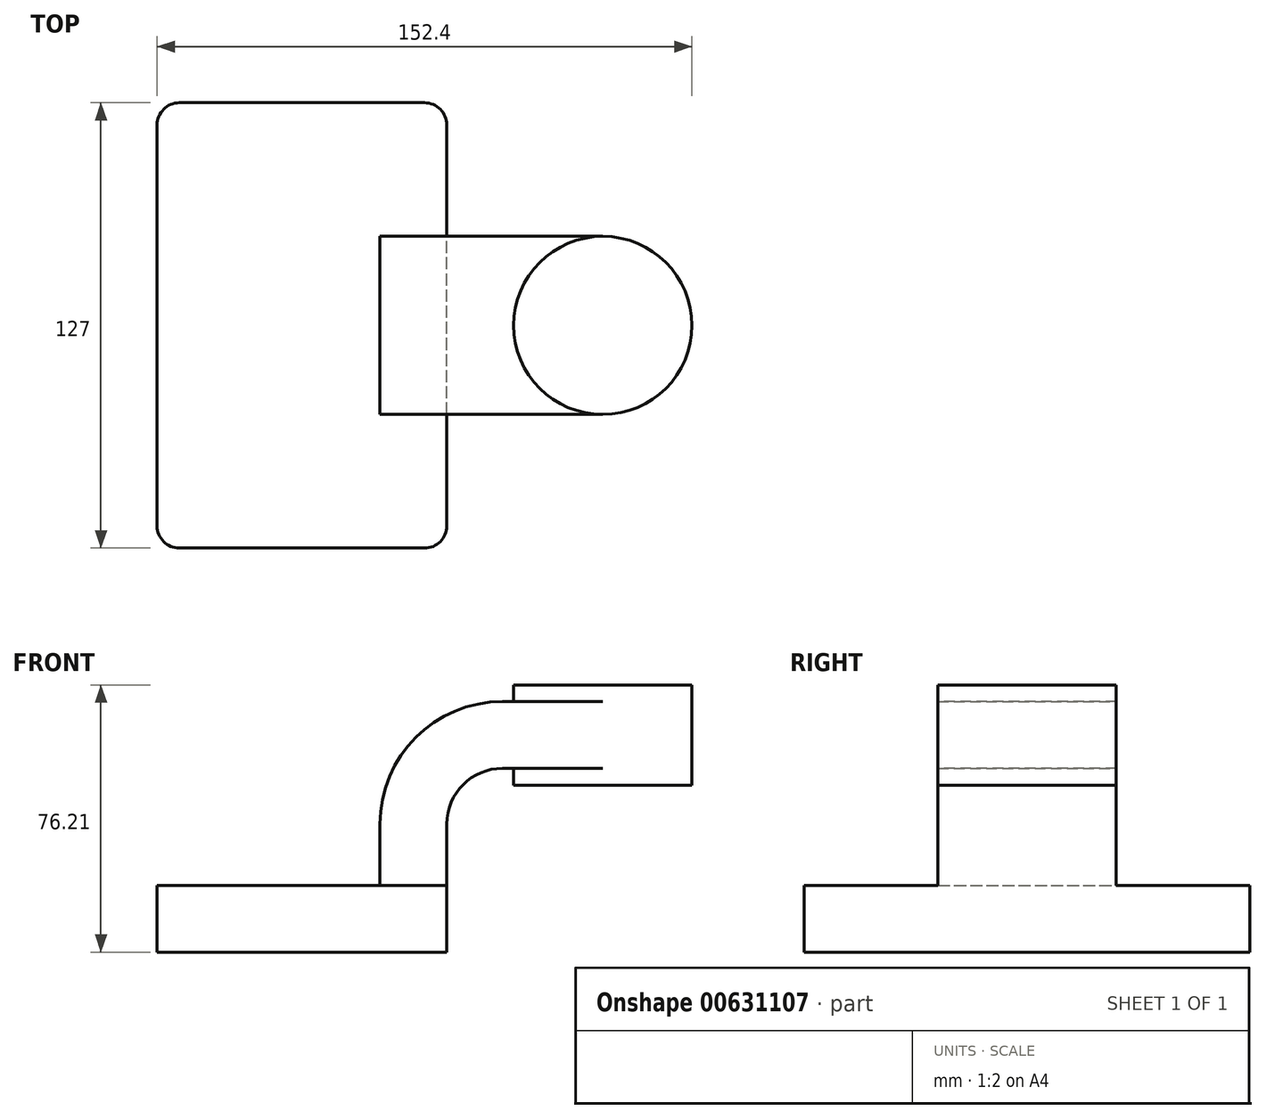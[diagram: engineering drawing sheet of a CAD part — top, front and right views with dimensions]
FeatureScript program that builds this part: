
annotation { "Feature Type Name" : "Feature", "Feature Type Description" : "" }
export const myFeature = defineFeature(function(context is Context, id is Id, definition is map)
    precondition{}
    {
        {
            var Q0;
            Q0=qCreatedBy(makeId("Front.planeOp"),FACE);
            var sketch = newSketch(context, id + "F0", { "sketchPlane" : qUnion([Q0])});
            skLineSegment(sketch, "E0.bottom", {"start": v(41.27, 9.53) * mm, "end": v(-41.28, 9.53) * mm});
            skLineSegment(sketch, "E0.top", {"start": v(41.28, -9.52) * mm, "end": v(-41.27, -9.52) * mm});
            skLineSegment(sketch, "E0.left", {"start": v(41.27, 9.53) * mm, "end": v(41.28, -9.52) * mm});
            skLineSegment(sketch, "E0.right", {"start": v(-41.28, 9.53) * mm, "end": v(-41.27, -9.52) * mm});
            skPoint(sketch, "E0.middle", {"position": v(0, 0) * mm});
            skLineSegment(sketch, "E1.bottom", {"start": v(111.12, 38.1) * mm, "end": v(60.32, 38.1) * mm});
            skLineSegment(sketch, "E1.top", {"start": v(111.12, 66.68) * mm, "end": v(60.32, 66.68) * mm});
            skLineSegment(sketch, "E1.left", {"start": v(111.12, 38.1) * mm, "end": v(111.12, 66.68) * mm});
            skLineSegment(sketch, "E1.right", {"start": v(60.32, 38.1) * mm, "end": v(60.32, 66.68) * mm});
            skPoint(sketch, "E1.middle", {"position": v(85.72, 52.39) * mm});
            skLineSegment(sketch, "E2", {"start": v(41.27, 9.53) * mm, "end": v(41.27, 27) * mm});
            skArc(sketch, "E3", {"start": v(41.27, 27) * mm, "mid": v(45.92, 38.23) * mm, "end": v(57.15, 42.88) * mm});
            skLineSegment(sketch, "E4", {"start": v(57.15, 42.88) * mm, "end": v(85.72, 42.88) * mm});
            skPoint(sketch, "E4.endSnap0", {"position": v(85.72, 66.68) * mm});
            skLineSegment(sketch, "E5.0", {"start": v(57.15, 61.93) * mm, "end": v(85.72, 61.93) * mm});
            skArc(sketch, "E5.1", {"start": v(22.22, 27) * mm, "mid": v(32.45, 51.7) * mm, "end": v(57.15, 61.93) * mm});
            skLineSegment(sketch, "E5.2", {"start": v(22.22, 9.53) * mm, "end": v(22.22, 27) * mm});
            skLineSegment(sketch, "E6", {"start": v(85.72, 66.68) * mm, "end": v(85.72, 38.1) * mm});
            skFitSpline(sketch, "E7", {"points": [v(-41.28, 9.53) * mm, v(57.15, 61.93) * mm], "startDerivative": vector(-0.14, 76.5) * mm, "endDerivative": vector(107.75, -0.35) * mm});
            skSolve(sketch);
        }
        {
            var Q0;
            Q0=makeQuery(id+"F0.imprint","IMPRINT",FACE,{"disambiguationData":[TD([[makeQuery(id+"F0.imprint","IMPRINT",EDGE,{"derivedFrom":sQuery(id+"F0.wireOp",EDGE,"E0.top")}),-1.0]])]});
            extrude(context, id + "F1", {"entities" : qUnion([Q0]), "endBound" : BoundingType.SYMMETRIC, "depth" : 127 * mm, "offsetDistance" : 25.4 * mm});
        }
        {
            var Q0;
            {var subQ1=sQuery(id+"F0.wireOp",EDGE,"E2");Q0=makeQuery(id+"F0.imprint","IMPRINT",FACE,{"disambiguationData":[TD([[makeQuery(id+"F0.imprint","IMPRINT",EDGE,{"derivedFrom":subQ1}),1.0]])]});}
            var Q1;
            {var subQ0=sQuery(id+"F0.wireOp",EDGE,"E4");var subQ1=sQuery(id+"F0.wireOp",EDGE,"E1.right");var subQ2=makeQuery(id+"F0.imprint","INTERSECT",VERTEX,{"derivedFrom":[subQ1,subQ0]});Q1=makeQuery(id+"F0.imprint","IMPRINT",FACE,{"disambiguationData":[TD([[makeQuery(id+"F0.imprint","IMPRINT",EDGE,{"disambiguationData":[TD([[subQ2,-1.0]])],"derivedFrom":subQ1}),-1.0]])]});}
            extrude(context, id + "F2", {"entities" : qUnion([Q0, Q1]), "operationType" : NewBodyOperationType.ADD, "endBound" : BoundingType.SYMMETRIC, "depth" : 50.8 * mm, "offsetDistance" : 25.4 * mm});
        }
        {
            var Q0;
            Q0=makeQuery(id+"F0.imprint","IMPRINT",FACE,{"disambiguationData":[TD([[makeQuery(id+"F0.imprint","IMPRINT",EDGE,{"derivedFrom":sQuery(id+"F0.wireOp",EDGE,"E5.1")}),1.0]])]});
            extrude(context, id + "F3", {"entities" : qUnion([Q0]), "operationType" : NewBodyOperationType.ADD, "endBound" : BoundingType.SYMMETRIC, "depth" : 15.88 * mm, "offsetDistance" : 25.4 * mm});
        }
        {
            var Q0;
            {var subQ4=sQuery(id+"F0.wireOp",EDGE,"E1.left");Q0=makeQuery(id+"F0.imprint","IMPRINT",FACE,{"disambiguationData":[TD([[makeQuery(id+"F0.imprint","IMPRINT",EDGE,{"derivedFrom":subQ4}),1.0]])]});}
            var Q1;
            Q1=sQuery(id+"F0.wireOp",EDGE,"E6");
            revolve(context, id + "F4", {"operationType" : NewBodyOperationType.ADD, "entities" : qUnion([Q0]), "axis" : qUnion([Q1]), "revolveType" : RevolveType.FULL});
        }
        {
            var Q0;
            Q0=makeQuery(id+"F1.opExtrude","CAP_EDGE",EDGE,{"disambiguationData":[OSD([sQuery(id+"F0.wireOp",EDGE,"E0.right")])],"isStart":false});
            var Q1;
            Q1=makeQuery(id+"F1.opExtrude","CAP_EDGE",EDGE,{"disambiguationData":[OSD([sQuery(id+"F0.wireOp",EDGE,"E0.left")])],"isStart":false});
            var Q2;
            Q2=makeQuery(id+"F1.opExtrude","CAP_EDGE",EDGE,{"disambiguationData":[OSD([sQuery(id+"F0.wireOp",EDGE,"E0.right")])],"isStart":true});
            var Q3;
            Q3=makeQuery(id+"F1.opExtrude","CAP_EDGE",EDGE,{"disambiguationData":[OSD([sQuery(id+"F0.wireOp",EDGE,"E0.left")])],"isStart":true});
            fillet(context, id + "F5", {"entities" : qUnion([Q0, Q1, Q2, Q3]), "radius" : 6.35 * mm, "tangentPropagation" : true, "allowEdgeOverflow" : false});
        }
    });
